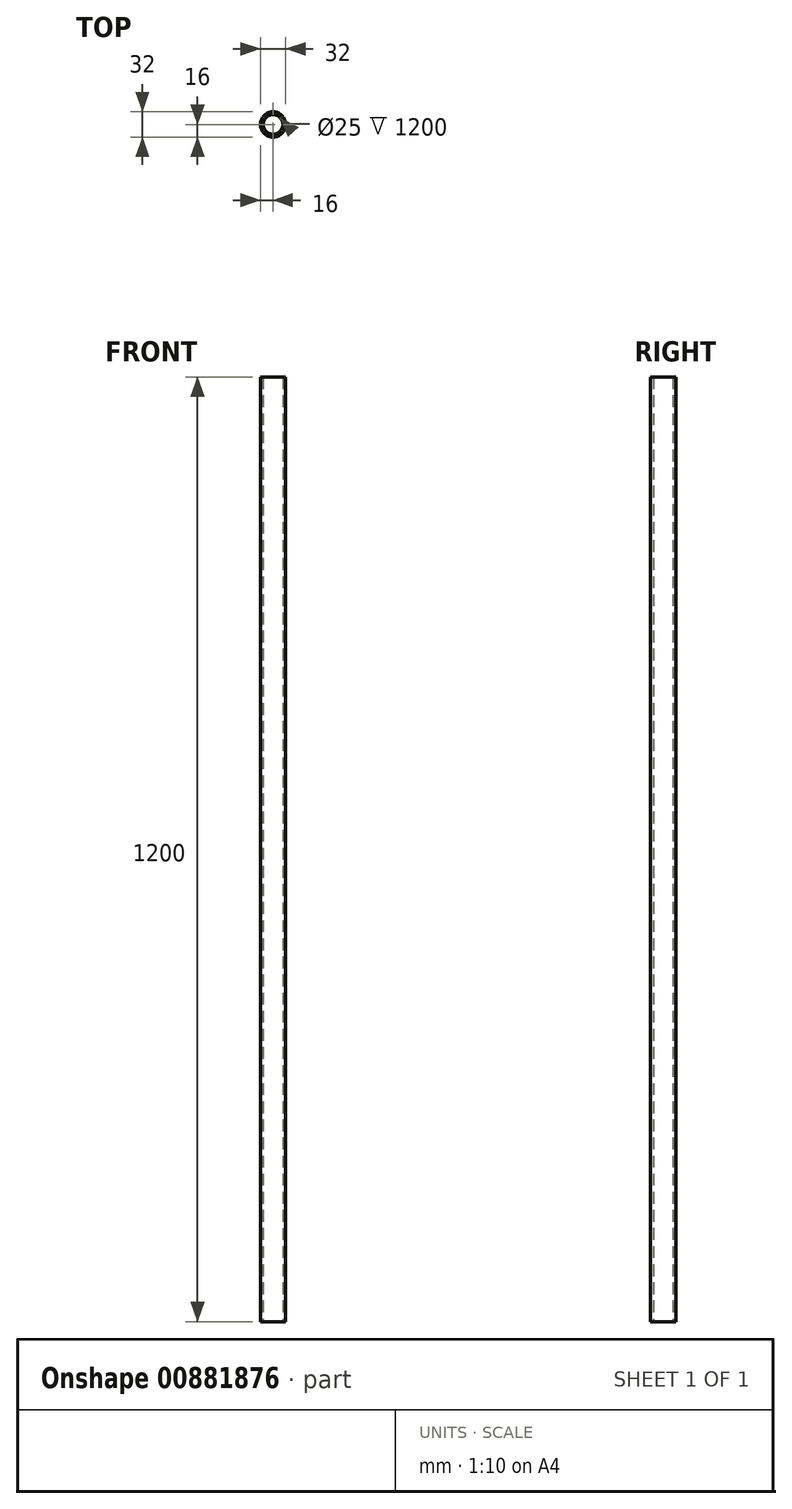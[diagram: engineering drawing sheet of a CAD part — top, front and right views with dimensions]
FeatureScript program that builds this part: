
annotation { "Feature Type Name" : "Feature", "Feature Type Description" : "" }
export const myFeature = defineFeature(function(context is Context, id is Id, definition is map)
    precondition{}
    {
        {
            var Q0;
            Q0=qCreatedBy(makeId("Top.planeOp"),FACE);
            var sketch = newSketch(context, id + "F0", { "sketchPlane" : qUnion([Q0])});
            skCircle(sketch, "E0", {"center": v(0, 0) * mm, "radius": 16 * mm});
            skCircle(sketch, "E1", {"center": v(0, 0) * mm, "radius": 12.5 * mm});
            skSolve(sketch);
        }
        {
            var Q0;
            Q0=qSketchRegion(id+"F0",true);
            extrude(context, id + "F1", {"entities" : qUnion([Q0]), "depth" : 1200 * mm, "offsetDistance" : 25 * mm});
        }
    });
